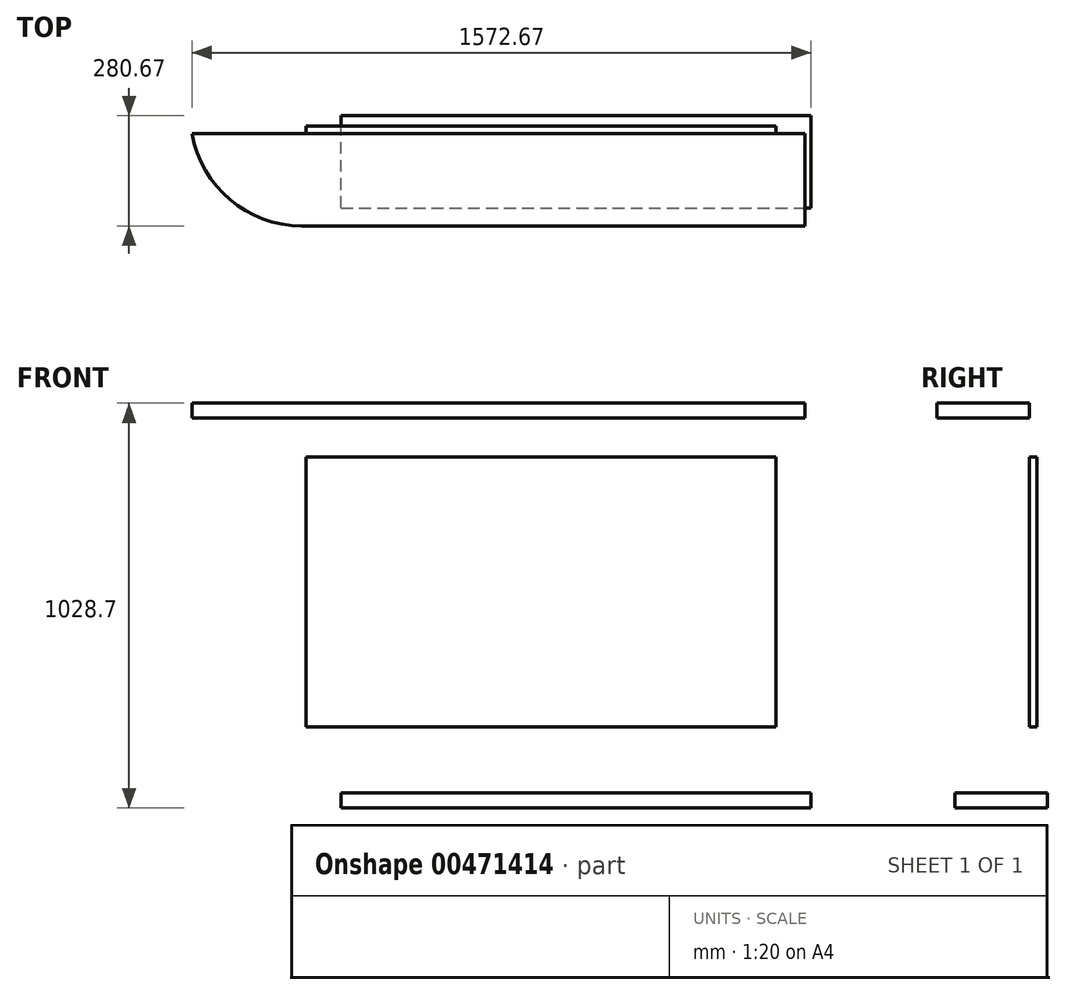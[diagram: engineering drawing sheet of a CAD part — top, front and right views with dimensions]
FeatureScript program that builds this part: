
annotation { "Feature Type Name" : "Feature", "Feature Type Description" : "" }
export const myFeature = defineFeature(function(context is Context, id is Id, definition is map)
    precondition{}
    {
        {
            var Q0;
            Q0=qCreatedBy(makeId("Front.planeOp"),FACE);
            var sketch = newSketch(context, id + "F0", { "sketchPlane" : qUnion([Q0])});
            skLineSegment(sketch, "E0.bottom", {"start": v(596.9, 342.9) * mm, "end": v(-596.9, 342.9) * mm});
            skLineSegment(sketch, "E0.top", {"start": v(596.9, -342.9) * mm, "end": v(-596.9, -342.9) * mm});
            skLineSegment(sketch, "E0.left", {"start": v(596.9, 342.9) * mm, "end": v(596.9, -342.9) * mm});
            skLineSegment(sketch, "E0.right", {"start": v(-596.9, 342.9) * mm, "end": v(-596.9, -342.9) * mm});
            skPoint(sketch, "E0.middle", {"position": v(0, 0) * mm});
            skSolve(sketch);
        }
        {
            var Q0;
            Q0 = qSketchRegion(id + "F0", true);
            extrude(context, id + "F1", {"entities" : qUnion([Q0]), "oppositeDirection" : true, "depth" : 19.05 * mm});
        }
        {
            var Q0;
            Q0=makeQuery(id+"F1.opExtrude","CAP_FACE",FACE,{"disambiguationData":[OSD([sQuery(id+"F0.wireOp",EDGE,"E0.bottom"),sQuery(id+"F0.wireOp",EDGE,"E0.top"),sQuery(id+"F0.wireOp",EDGE,"E0.left"),sQuery(id+"F0.wireOp",EDGE,"E0.right")])],"isStart":true});
            var sketch = newSketch(context, id + "F2", { "sketchPlane" : qUnion([Q0])});
            skLineSegment(sketch, "E1.bottom", {"start": v(-1717.21, 479.92) * mm, "end": v(-523.41, 479.92) * mm});
            skLineSegment(sketch, "E1.top", {"start": v(-1717.21, 441.82) * mm, "end": v(-523.41, 441.82) * mm});
            skLineSegment(sketch, "E1.left", {"start": v(-1717.21, 479.92) * mm, "end": v(-1717.21, 441.82) * mm});
            skLineSegment(sketch, "E1.right", {"start": v(-523.41, 479.92) * mm, "end": v(-523.41, 441.82) * mm});
            skSolve(sketch);
        }
        {
            var Q0;
            Q0=makeQuery(id+"F2.imprint","IMPRINT",FACE,{"disambiguationData":[TD([[makeQuery(id+"F2.imprint","IMPRINT",EDGE,{"derivedFrom":sQuery(id+"F2.wireOp",EDGE,"E1.bottom")}),-1.0]])]});
            extrude(context, id + "F3", {"entities" : qUnion([Q0]), "depth" : 234.95 * mm});
        }
        {
            var Q0;
            Q0=makeQuery(id+"F3.opExtrude","SWEPT_BODY",BODY,{"disambiguationData":[OSD([sQuery(id+"F2.wireOp",EDGE,"E1.bottom"),sQuery(id+"F2.wireOp",EDGE,"E1.top"),sQuery(id+"F2.wireOp",EDGE,"E1.left"),sQuery(id+"F2.wireOp",EDGE,"E1.right")])]});
            transform(context, id + "F4", {"entities" : qUnion([Q0]), "transformType" : TransformType.TRANSLATION_3D, "dx" : 0 * mm, "dy" : 0 * mm, "dz" : 0 * mm, "makeCopy" : true});
        }
        {
            var Q0;
            Q0=makeQuery(id+"F3.opExtrude","SWEPT_BODY",BODY,{"disambiguationData":[OSD([sQuery(id+"F2.wireOp",EDGE,"E1.bottom"),sQuery(id+"F2.wireOp",EDGE,"E1.top"),sQuery(id+"F2.wireOp",EDGE,"E1.left"),sQuery(id+"F2.wireOp",EDGE,"E1.right")])]});
            transform(context, id + "F5", {"entities" : qUnion([Q0]), "transformType" : TransformType.TRANSLATION_3D, "dx" : 1209.04 * mm, "dy" : -220.98 * mm, "dz" : -1148.08 * mm, "makeCopy" : true});
        }
        {
            var Q0;
            Q0=makeQuery(id+"F4.opPattern","COPY",BODY,{"derivedFrom":makeQuery(id+"F3.opExtrude","SWEPT_BODY",BODY,{"disambiguationData":[OSD([sQuery(id+"F2.wireOp",EDGE,"E1.bottom"),sQuery(id+"F2.wireOp",EDGE,"E1.top"),sQuery(id+"F2.wireOp",EDGE,"E1.left"),sQuery(id+"F2.wireOp",EDGE,"E1.right")])]}),"instanceName":"1"});
            deleteBodies(context, id + "F6", {"entities" : qUnion([Q0])});
        }
        {
            var Q0;
            Q0=makeQuery(id+"F3.opExtrude","SWEPT_BODY",BODY,{"disambiguationData":[OSD([sQuery(id+"F2.wireOp",EDGE,"E1.bottom"),sQuery(id+"F2.wireOp",EDGE,"E1.top"),sQuery(id+"F2.wireOp",EDGE,"E1.left"),sQuery(id+"F2.wireOp",EDGE,"E1.right")])]});
            transform(context, id + "F7", {"entities" : qUnion([Q0]), "transformType" : TransformType.TRANSLATION_3D, "dx" : 1193.8 * mm, "dy" : 0 * mm, "dz" : 0 * mm, "makeCopy" : false});
        }
        {
            var Q0;
            Q0=makeQuery(id+"F5.opPattern","COPY",BODY,{"derivedFrom":makeQuery(id+"F3.opExtrude","SWEPT_BODY",BODY,{"disambiguationData":[OSD([sQuery(id+"F2.wireOp",EDGE,"E1.bottom"),sQuery(id+"F2.wireOp",EDGE,"E1.top"),sQuery(id+"F2.wireOp",EDGE,"E1.left"),sQuery(id+"F2.wireOp",EDGE,"E1.right")])]}),"instanceName":"1"});
            transform(context, id + "F8", {"entities" : qUnion([Q0]), "transformType" : TransformType.TRANSLATION_3D, "dx" : 0 * mm, "dy" : 266.7 * mm, "dz" : 157.48 * mm, "makeCopy" : false});
        }
        {
            var Q0;
            Q0=makeQuery(id+"F3.opExtrude","SWEPT_FACE",FACE,{"disambiguationData":[OSD([sQuery(id+"F2.wireOp",EDGE,"E1.top")])]});
            var sketch = newSketch(context, id + "F9", { "sketchPlane" : qUnion([Q0])});
            skLineSegment(sketch, "E2", {"start": v(-523.41, 234.95) * mm, "end": v(-608.15, 234.95) * mm});
            skLineSegment(sketch, "E3", {"start": v(-523.41, 0) * mm, "end": v(-887.04, 0) * mm});
            skArc(sketch, "E4", {"start": v(-608.15, 234.95) * mm, "mid": v(-790.48, 168.38) * mm, "end": v(-887.04, 0) * mm});
            skSolve(sketch);
        }
        {
            var Q0;
            Q0=makeQuery(id+"F9.imprint","IMPRINT",FACE,{"disambiguationData":[TD([[makeQuery(id+"F9.imprint","IMPRINT",EDGE,{"derivedFrom":sQuery(id+"F9.wireOp",EDGE,"E2")}),1.0]])]});
            extrude(context, id + "F10", {"entities" : qUnion([Q0]), "operationType" : NewBodyOperationType.ADD, "oppositeDirection" : true, "depth" : 38.1 * mm});
        }
    });
